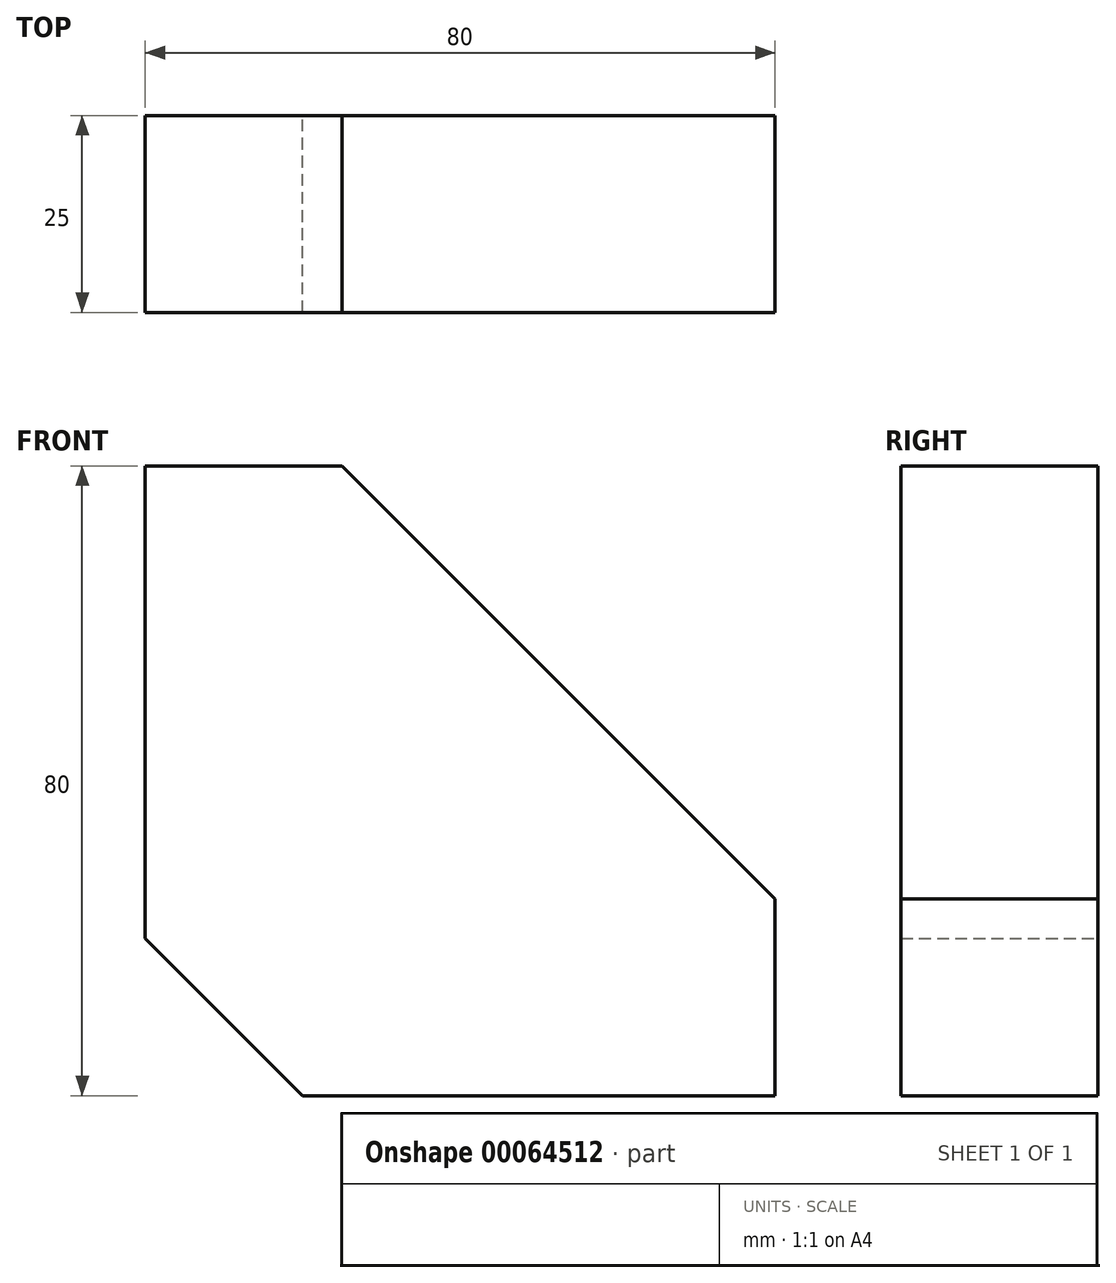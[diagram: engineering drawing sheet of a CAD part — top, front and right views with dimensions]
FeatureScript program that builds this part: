
annotation { "Feature Type Name" : "Feature", "Feature Type Description" : "" }
export const myFeature = defineFeature(function(context is Context, id is Id, definition is map)
    precondition{}
    {
        {
            var Q0;
            Q0=qCreatedBy(makeId("Front.planeOp"),FACE);
            var sketch = newSketch(context, id + "F0", { "sketchPlane" : qUnion([Q0])});
            skLineSegment(sketch, "E0.bottom", {"start": v(2470, 0) * mm, "end": v(2530, 0) * mm});
            skLineSegment(sketch, "E0.top", {"start": v(2450, 80) * mm, "end": v(2475, 80) * mm});
            skLineSegment(sketch, "E0.right", {"start": v(2530, 0) * mm, "end": v(2530, 25) * mm});
            skLineSegment(sketch, "E1", {"start": v(2475, 80) * mm, "end": v(2530, 25) * mm});
            skLineSegment(sketch, "E2", {"start": v(2450, 80) * mm, "end": v(2450, 20) * mm});
            skLineSegment(sketch, "E3", {"start": v(2450, 20) * mm, "end": v(2470, 0) * mm});
            skPoint(sketch, "E4", {"position": v(2450, 0) * mm});
            skSolve(sketch);
        }
        {
            var Q0;
            Q0=makeQuery(id+"F0.imprint","IMPRINT",FACE,{"disambiguationData":[TD([[makeQuery(id+"F0.imprint","IMPRINT",EDGE,{"derivedFrom":sQuery(id+"F0.wireOp",EDGE,"E0.bottom")}),1.0]])]});
            extrude(context, id + "F1", {"entities" : qUnion([Q0]), "endBound" : BoundingType.SYMMETRIC, "depth" : 25 * mm});
        }
        {
            var Q0;
            Q0=makeQuery(id+"F1.opExtrude","SWEPT_BODY",BODY,{"disambiguationData":[OSD([sQuery(id+"F0.wireOp",EDGE,"E0.bottom"),sQuery(id+"F0.wireOp",EDGE,"E0.top"),sQuery(id+"F0.wireOp",EDGE,"E0.left"),sQuery(id+"F0.wireOp",EDGE,"E0.right"),sQuery(id+"F0.wireOp",EDGE,"E1")])]});
            transform(context, id + "F2", {"entities" : qUnion([Q0]), "transformType" : TransformType.TRANSLATION_3D, "dx" : 0 * mm, "dy" : 0 * mm, "dz" : 0 * mm, "makeCopy" : true});
        }
        {
            var Q0;
            Q0=makeQuery(id+"F2.opPattern","COPY",BODY,{"derivedFrom":makeQuery(id+"F1.opExtrude","SWEPT_BODY",BODY,{"disambiguationData":[OSD([sQuery(id+"F0.wireOp",EDGE,"E0.bottom"),sQuery(id+"F0.wireOp",EDGE,"E0.top"),sQuery(id+"F0.wireOp",EDGE,"E0.left"),sQuery(id+"F0.wireOp",EDGE,"E0.right"),sQuery(id+"F0.wireOp",EDGE,"E1")])]}),"instanceName":"1"});
            deleteBodies(context, id + "F3", {"entities" : qUnion([Q0])});
        }
    });
